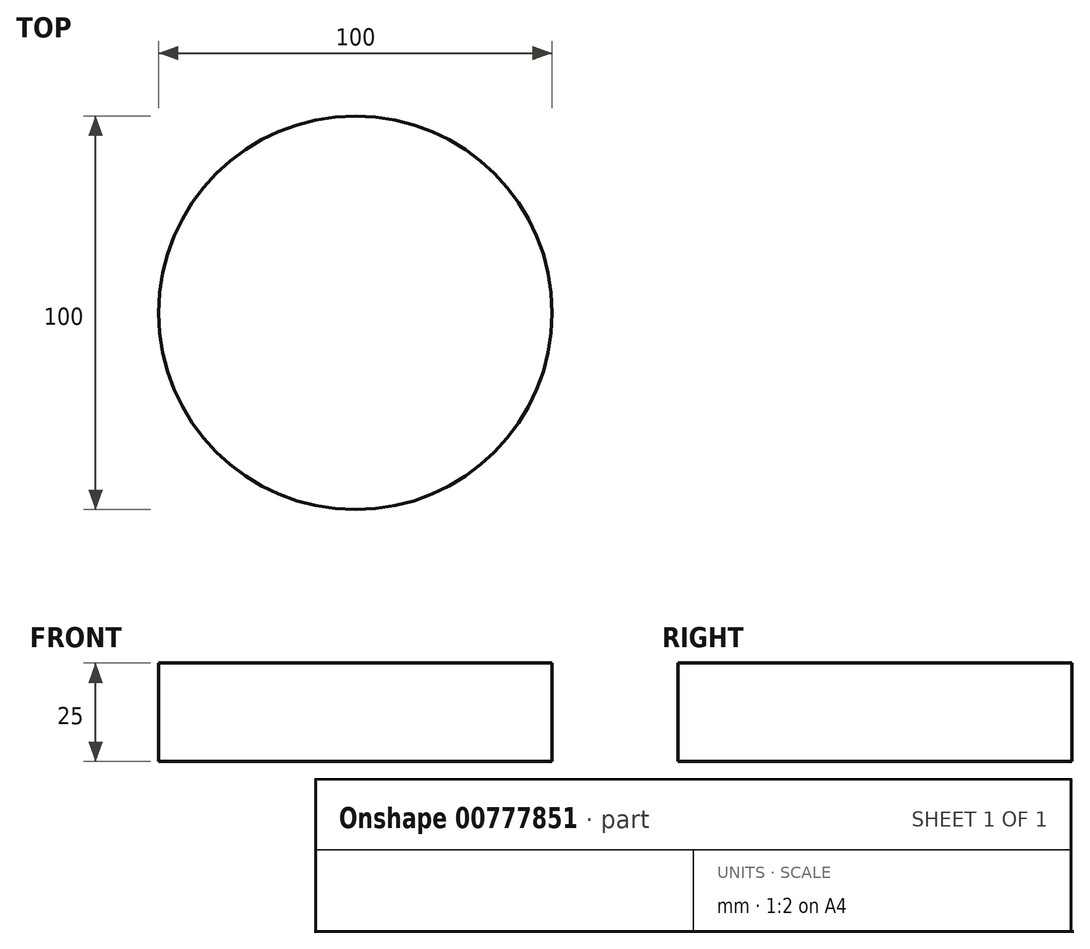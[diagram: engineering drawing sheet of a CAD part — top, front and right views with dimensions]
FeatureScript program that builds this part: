
annotation { "Feature Type Name" : "Feature", "Feature Type Description" : "" }
export const myFeature = defineFeature(function(context is Context, id is Id, definition is map)
    precondition{}
    {
        {
            var Q0;
            Q0=qCreatedBy(makeId("Top.planeOp"),FACE);
            var sketch = newSketch(context, id + "F0", { "sketchPlane" : qUnion([Q0])});
            skCircle(sketch, "E0", {"center": v(0, 0) * mm, "radius": 50 * mm});
            skSolve(sketch);
        }
        {
            var Q0;
            Q0 = qSketchRegion(id + "F0", true);
            extrude(context, id + "F1", {"entities" : qUnion([Q0]), "depth" : 25 * mm, "offsetDistance" : 25 * mm});
        }
    });
